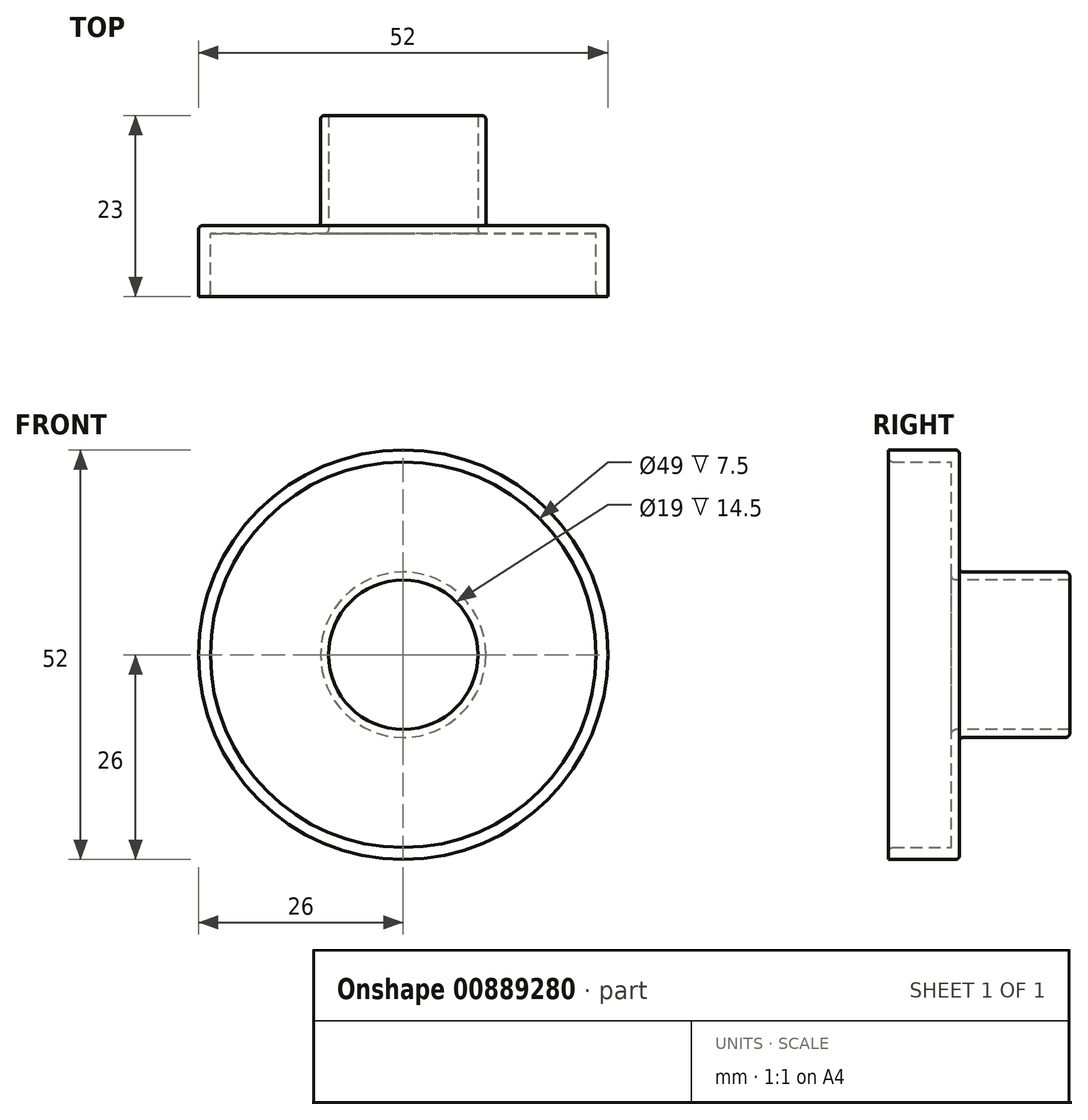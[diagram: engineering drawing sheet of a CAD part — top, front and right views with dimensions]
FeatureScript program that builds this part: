
annotation { "Feature Type Name" : "Feature", "Feature Type Description" : "" }
export const myFeature = defineFeature(function(context is Context, id is Id, definition is map)
    precondition{}
    {
        {
            var Q0;
            Q0=qCreatedBy(makeId("Front.planeOp"),FACE);
            var sketch = newSketch(context, id + "F0", { "sketchPlane" : qUnion([Q0])});
            skCircle(sketch, "E0", {"center": v(0, 0) * mm, "radius": 24.5 * mm});
            skCircle(sketch, "E1", {"center": v(0, 0) * mm, "radius": 26 * mm});
            skSolve(sketch);
        }
        {
            var Q0;
            Q0 = qSketchRegion(id + "F0", true);
            extrude(context, id + "F1", {"entities" : qUnion([Q0]), "depth" : 8 * mm, "offsetDistance" : 25 * mm});
        }
        {
            var Q0;
            Q0=qCreatedBy(makeId("Front.planeOp"),FACE);
            var sketch = newSketch(context, id + "F2", { "sketchPlane" : qUnion([Q0])});
            skCircle(sketch, "E2", {"center": v(0, 0) * mm, "radius": 26 * mm});
            skCircle(sketch, "E3", {"center": v(0, 0) * mm, "radius": 9.5 * mm});
            skSolve(sketch);
        }
        {
            var Q0;
            Q0 = qSketchRegion(id + "F2", true);
            extrude(context, id + "F3", {"entities" : qUnion([Q0]), "operationType" : NewBodyOperationType.ADD, "oppositeDirection" : true, "depth" : 1 * mm, "offsetDistance" : 25 * mm});
        }
        {
            var Q0;
            Q0=qCreatedBy(makeId("Front.planeOp"),FACE);
            var sketch = newSketch(context, id + "F4", { "sketchPlane" : qUnion([Q0])});
            skCircle(sketch, "E4", {"center": v(0, 0) * mm, "radius": 9.5 * mm});
            skCircle(sketch, "E5", {"center": v(0, 0) * mm, "radius": 10.5 * mm});
            skSolve(sketch);
        }
        {
            var Q0;
            Q0 = qSketchRegion(id + "F4", true);
            extrude(context, id + "F5", {"entities" : qUnion([Q0]), "operationType" : NewBodyOperationType.ADD, "oppositeDirection" : true, "depth" : 15 * mm, "offsetDistance" : 25 * mm});
        }
        {
            var Q0;
            Q0=makeQuery(id+"F3.opExtrude","CAP_EDGE",EDGE,{"disambiguationData":[OSD([sQuery(id+"F2.wireOp",EDGE,"E2")])],"isStart":false});
            var Q1;
            Q1=makeQuery(id+"F5.boolean.opBoolean","INTERSECT",EDGE,{"derivedFrom":[makeQuery(id+"F3.opExtrude","CAP_FACE",FACE,{"disambiguationData":[OSD([sQuery(id+"F2.wireOp",EDGE,"E2"),sQuery(id+"F2.wireOp",EDGE,"E3")])],"isStart":false}),makeQuery(id+"F5.opExtrude","SWEPT_FACE",FACE,{"disambiguationData":[OSD([sQuery(id+"F4.wireOp",EDGE,"E5")])]})]});
            var Q2;
            Q2=makeQuery(id+"F5.opExtrude","CAP_EDGE",EDGE,{"disambiguationData":[OSD([sQuery(id+"F4.wireOp",EDGE,"E5")])],"isStart":false});
            var Q3;
            Q3=makeQuery(id+"F1.opExtrude","CAP_EDGE",EDGE,{"disambiguationData":[OSD([sQuery(id+"F0.wireOp",EDGE,"E0")])],"isStart":false});
            var Q4;
            Q4=makeQuery(id+"F3.opExtrude","CAP_EDGE",EDGE,{"disambiguationData":[OSD([sQuery(id+"F2.wireOp",EDGE,"E3")])],"isStart":true});
            fillet(context, id + "F6", {"entities" : qUnion([Q0, Q1, Q2, Q3, Q4]), "radius" : 0.5 * mm, "tangentPropagation" : true, "allowEdgeOverflow" : false});
        }
    });
